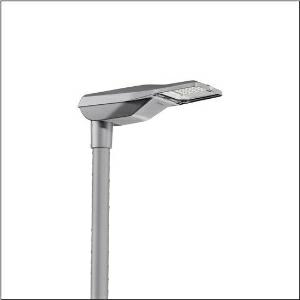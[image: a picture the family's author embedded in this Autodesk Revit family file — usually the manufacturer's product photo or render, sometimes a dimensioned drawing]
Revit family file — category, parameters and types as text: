
# Revit family: streetlight_sl_21_iq_micro___p0_5a_5xe1v31d08cb_9f45
name_source: partatom
category: Lighting Fixtures
units: mm (PartAtom-declared; Revit-internal decimal feet)

## family parameters
Cut with Voids When Loaded = No
Host = Face
Light Source = No
Part Type = Normal
Room Calculation Point = No
Round Connector Dimension = Use Diameter
Shared = No

## types (1)
- --- (1 x LED, 2780 lm, 19.4 W, 3000K)
    Apparent Load = 19 VA
    CIE Flux Codes = 37 73 96 100 100
    Color Rendering = 70
    Color Temperature = 3000K
    Default Elevation = 1800 mm
    Description = Streetlight SL 21 iQ micro, mast luminaire, primary light control with lens, of PMMA, primary optical cover: cover, of toughened safety glass, transparent, light distribution: P0.5a, light emission: direct distribution, primary light characteristic: asymmetric, installation type: post-top, side-entry, LED, High Power LED, rated luminous flux: 2.780lm, luminous efficacy: 143lm/W, light colour: 730, colour temperature: 3000K, control gear: iQ-Comfort, control: pre-setting: linear dimming characteristic, Auto-Match, Temp-Guard, Lumen-Switch, Night-Set, Smart-Wire, Light-Fading, Desk-Remote (wireless, voltage-free reading and setting of iQ features in the workshop via application-optimized NFC function/RFID function), optimised constant luminous flux control (CLO 2.0), mains connection: 220..240V, AC, 50/60Hz, start of lifetime: 19W, end of service life: 20W, reduction: 10W, luminaire housing, of diecast aluminium, powder-coated, SITECO metallic grey (DB 702S), corrosivity category C5 high according to DIN EN ISO 12944, please order mast flange separately, inclination adjustable: 0°, 5°, 10°, 15°, sealing non-destructively replaceable, multi-level sealing system, length: 528mm, width: 235mm, height: 110mm, mast flange for spigot size: 42mm (side-entry): 5XC10008XM4, 60/48mm (side-entry/post-top): 5XC10108XM2, 76/60mm (side-entry/post-top): 5XC10108XM1, protection rating (complete): IP66, insulation class (complete): insulation class II (safety insulation), certification: CE, ENEC, ENEC+, VDE, impact resistance: IK10, permissible operating ambient temperature for outdoor applications: -40..+50°C, standard-compliant lighting for roads and squares, packaging unit: 1 piece

Light Distribution: P0.5a
    Height = 110 mm
    Lamp = 1 x LED
    Lamp Light Flux = 2780 lm
    Lamp Power = 19.4 W
    Lamp count = 1
    Length = 528 mm
    Luminous efficacy = 143 lm/W
    Manufacturer = Siteco
    ModVariant = No
    Model = 5XE1V31D08CB
    Number of Poles = 1
    OnlyDefault = Yes
    Power Factor = 1
    Product Name = Streetlight SL 21 iQ micro | P0.5a
    Product group = mast luminaire | pylon top
    ProductGroupID = 6100
    Protection Class = Protection class II
    Protection Degree = IP 66
    RLX_Detail_Level = 1
    RLX_Emergency_Light_Flux = 0 lm
    RLX_Emergency_Type = 0
    RLX_Emergency_Type_DB = No
    RlxData = <blob elided: 97825 chars, md5=2e4d4a87>
    Socket = socket
    Standby Power = 0 W
    System Light Flux = 2780 lm
    System Power = 19 W
    Type Comments = factory setting: luminous flux: 100 % | dim-lin: 254 | 387 mA
    Type Image = l_1006881.jpg
    URL = http://relux.com
    VarID = @adj_078071
    Voltage = 0 V
    Weight = 0.00 kg
    Width = 235 mm

## geometry (parser evidence)
native form markers: Blend x4, Sweep x9
no freeform markers — native parametric forms only
